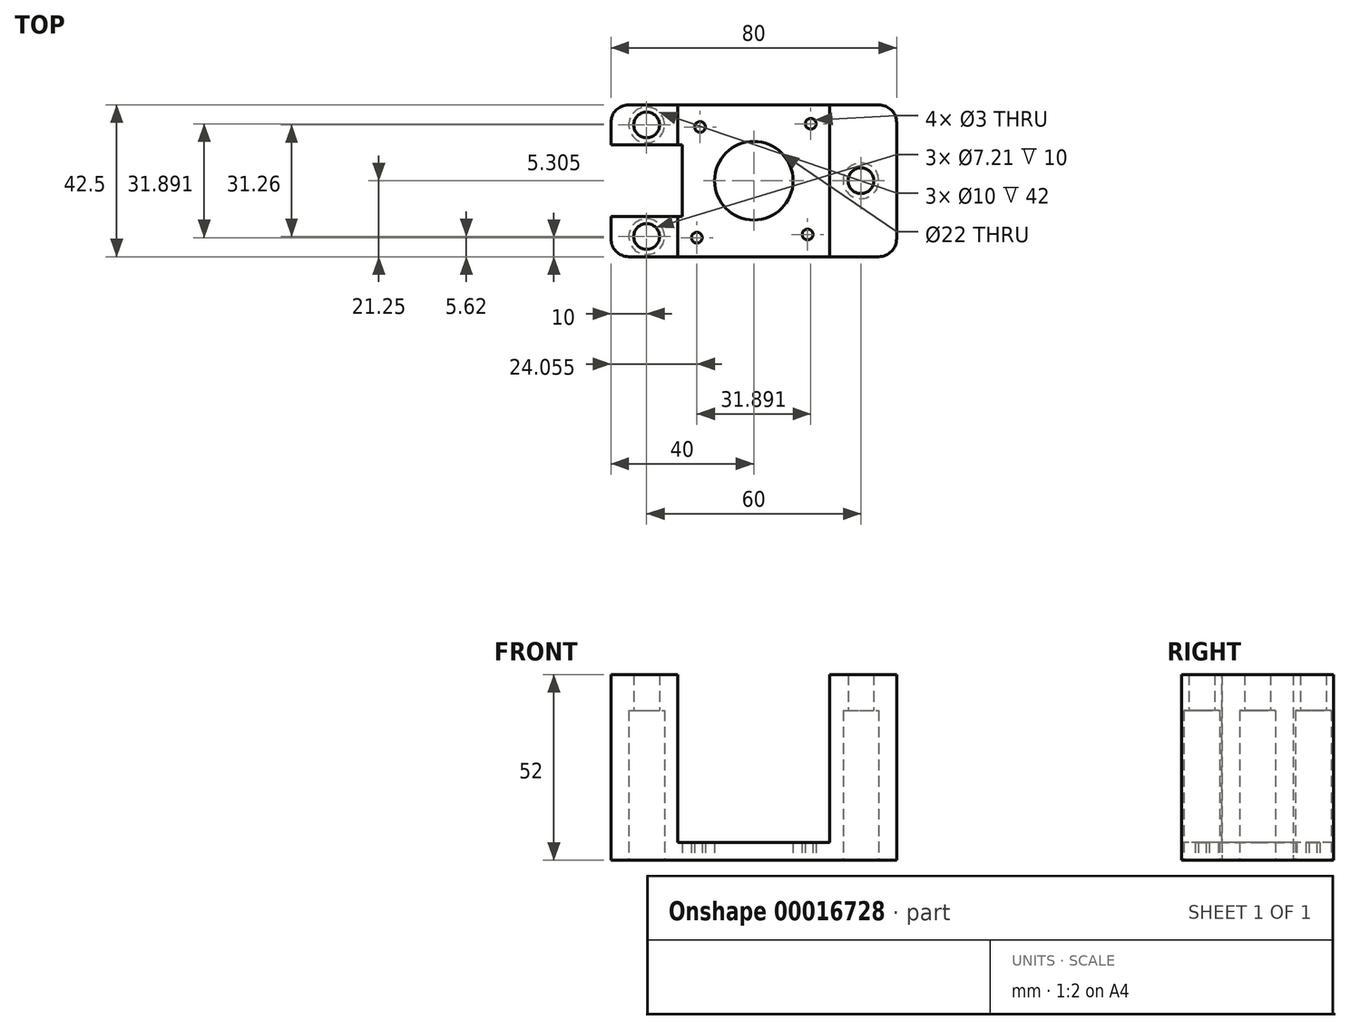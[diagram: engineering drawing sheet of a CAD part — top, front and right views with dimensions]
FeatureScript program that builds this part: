
annotation { "Feature Type Name" : "Feature", "Feature Type Description" : "" }
export const myFeature = defineFeature(function(context is Context, id is Id, definition is map)
    precondition{}
    {
        {
            var Q0;
            Q0=qCreatedBy(makeId("Top.planeOp"),FACE);
            var sketch = newSketch(context, id + "F0", { "sketchPlane" : qUnion([Q0])});
            skLineSegment(sketch, "E0.bottom", {"start": v(-21.25, 21.25) * mm, "end": v(21.25, 21.25) * mm, "construction": true});
            skLineSegment(sketch, "E0.top", {"start": v(-21.25, -21.25) * mm, "end": v(21.25, -21.25) * mm, "construction": true});
            skLineSegment(sketch, "E0.left", {"start": v(-21.25, 21.25) * mm, "end": v(-21.25, -21.25) * mm, "construction": true});
            skLineSegment(sketch, "E0.right", {"start": v(21.25, 21.25) * mm, "end": v(21.25, -21.25) * mm, "construction": true});
            skLineSegment(sketch, "E1", {"start": v(-21.25, 21.25) * mm, "end": v(21.25, -21.25) * mm, "construction": true});
            skLineSegment(sketch, "E2", {"start": v(21.25, 21.25) * mm, "end": v(-21.25, -21.25) * mm, "construction": true});
            skCircle(sketch, "E3", {"center": v(-15.05, 15.05) * mm, "radius": 1.5 * mm});
            skCircle(sketch, "E4", {"center": v(-15.95, -15.95) * mm, "radius": 1.5 * mm});
            skCircle(sketch, "E5", {"center": v(15.05, -15.05) * mm, "radius": 1.5 * mm});
            skCircle(sketch, "E6", {"center": v(15.95, 15.95) * mm, "radius": 1.5 * mm});
            skLineSegment(sketch, "E7", {"start": v(40, 21.25) * mm, "end": v(40, -21.25) * mm});
            skLineSegment(sketch, "E8", {"start": v(40, -21.25) * mm, "end": v(-40, -21.25) * mm});
            skLineSegment(sketch, "E9", {"start": v(-40, -21.25) * mm, "end": v(-40, -10) * mm});
            skLineSegment(sketch, "E10", {"start": v(-40, -10) * mm, "end": v(-20, -10) * mm});
            skLineSegment(sketch, "E11", {"start": v(-20, -10) * mm, "end": v(-20, 10) * mm});
            skLineSegment(sketch, "E12", {"start": v(-20, 10) * mm, "end": v(-40, 10) * mm});
            skLineSegment(sketch, "E13", {"start": v(-40, 10) * mm, "end": v(-40, 21.25) * mm});
            skLineSegment(sketch, "E14", {"start": v(-40, 21.25) * mm, "end": v(40, 21.25) * mm});
            skCircle(sketch, "E15", {"center": v(0, 0) * mm, "radius": 11 * mm});
            skCircle(sketch, "E16", {"center": v(30, 0) * mm, "radius": 3.6 * mm});
            skCircle(sketch, "E17", {"center": v(-30, -15.63) * mm, "radius": 3.6 * mm});
            skCircle(sketch, "E18", {"center": v(-30, 15.63) * mm, "radius": 3.6 * mm});
            skLineSegment(sketch, "E19", {"start": v(0, 0) * mm, "end": v(40, 0) * mm, "construction": true});
            skLineSegment(sketch, "E20", {"start": v(40, 21.25) * mm, "end": v(-40, -21.25) * mm, "construction": true});
            skLineSegment(sketch, "E21", {"start": v(-40, 21.25) * mm, "end": v(40, -21.25) * mm, "construction": true});
            skCircle(sketch, "E22", {"center": v(30, 0) * mm, "radius": 5 * mm, "construction": true});
            skCircle(sketch, "E23", {"center": v(-30, -15.63) * mm, "radius": 5 * mm, "construction": true});
            skCircle(sketch, "E24", {"center": v(-30, 15.63) * mm, "radius": 5 * mm, "construction": true});
            skSolve(sketch);
        }
        {
            var Q0;
            Q0 = qSketchRegion(id + "F0", true);
            extrude(context, id + "F1", {"entities" : qUnion([Q0]), "depth" : 52 * mm});
        }
        {
            var Q0;
            Q0=makeQuery(id+"F1.opExtrude","SWEPT_FACE",FACE,{"disambiguationData":[OSD([sQuery(id+"F0.wireOp",EDGE,"E8")])]});
            var sketch = newSketch(context, id + "F2", { "sketchPlane" : qUnion([Q0])});
            skPoint(sketch, "E25.0", {"position": v(-21.25, 0) * mm});
            skLineSegment(sketch, "E26.bottom", {"start": v(-21.25, 52) * mm, "end": v(21.25, 52) * mm});
            skLineSegment(sketch, "E26.top", {"start": v(-21.25, 5) * mm, "end": v(21.25, 5) * mm});
            skLineSegment(sketch, "E26.left", {"start": v(-21.25, 52) * mm, "end": v(-21.25, 5) * mm});
            skLineSegment(sketch, "E26.right", {"start": v(21.25, 52) * mm, "end": v(21.25, 5) * mm});
            skLineSegment(sketch, "E27", {"start": v(-21.25, 0) * mm, "end": v(-21.25, 5) * mm, "construction": true});
            skSolve(sketch);
        }
        {
            var Q0;
            Q0 = qSketchRegion(id + "F2", true);
            extrude(context, id + "F3", {"entities" : qUnion([Q0]), "operationType" : NewBodyOperationType.REMOVE, "endBound" : BoundingType.THROUGH_ALL, "oppositeDirection" : true, "depth" : 25 * mm});
        }
        {
            var Q0;
            Q0=makeQuery(id+"F1.opExtrude","SWEPT_EDGE",EDGE,{"disambiguationData":[OSD([sQuery(id+"F0.wireOp",EDGE,"E8"),sQuery(id+"F0.wireOp",EDGE,"E9")])]});
            var Q1;
            Q1=makeQuery(id+"F1.opExtrude","SWEPT_EDGE",EDGE,{"disambiguationData":[OSD([sQuery(id+"F0.wireOp",EDGE,"E13"),sQuery(id+"F0.wireOp",EDGE,"E14")])]});
            var Q2;
            Q2=makeQuery(id+"F1.opExtrude","SWEPT_EDGE",EDGE,{"disambiguationData":[OSD([sQuery(id+"F0.wireOp",EDGE,"E7"),sQuery(id+"F0.wireOp",EDGE,"E8")])]});
            var Q3;
            Q3=makeQuery(id+"F1.opExtrude","SWEPT_EDGE",EDGE,{"disambiguationData":[OSD([sQuery(id+"F0.wireOp",EDGE,"E7"),sQuery(id+"F0.wireOp",EDGE,"E14")])]});
            fillet(context, id + "F4", {"entities" : qUnion([Q0, Q1, Q2, Q3]), "radius" : 5 * mm, "tangentPropagation" : true, "allowEdgeOverflow" : false});
        }
        {
            var Q0;
            Q0=makeQuery(id+"F1.opExtrude","CAP_FACE",FACE,{"disambiguationData":[OSD([sQuery(id+"F0.wireOp",EDGE,"E3"),sQuery(id+"F0.wireOp",EDGE,"E4"),sQuery(id+"F0.wireOp",EDGE,"E5"),sQuery(id+"F0.wireOp",EDGE,"E6"),sQuery(id+"F0.wireOp",EDGE,"E7"),sQuery(id+"F0.wireOp",EDGE,"E8"),sQuery(id+"F0.wireOp",EDGE,"E9"),sQuery(id+"F0.wireOp",EDGE,"E10"),sQuery(id+"F0.wireOp",EDGE,"E11"),sQuery(id+"F0.wireOp",EDGE,"E12"),sQuery(id+"F0.wireOp",EDGE,"E13"),sQuery(id+"F0.wireOp",EDGE,"E14"),sQuery(id+"F0.wireOp",EDGE,"E15"),sQuery(id+"F0.wireOp",EDGE,"E16"),sQuery(id+"F0.wireOp",EDGE,"E17"),sQuery(id+"F0.wireOp",EDGE,"E18")])],"isStart":true});
            var sketch = newSketch(context, id + "F5", { "sketchPlane" : qUnion([Q0])});
            skCircle(sketch, "E28", {"center": v(-30, -15.63) * mm, "radius": 5 * mm});
            skCircle(sketch, "E29", {"center": v(-30, 15.63) * mm, "radius": 5 * mm});
            skCircle(sketch, "E30", {"center": v(30, 0) * mm, "radius": 5 * mm});
            skSolve(sketch);
        }
        {
            var Q0;
            Q0 = qSketchRegion(id + "F5", true);
            extrude(context, id + "F6", {"entities" : qUnion([Q0]), "operationType" : NewBodyOperationType.REMOVE, "oppositeDirection" : true, "depth" : 42 * mm});
        }
    });
